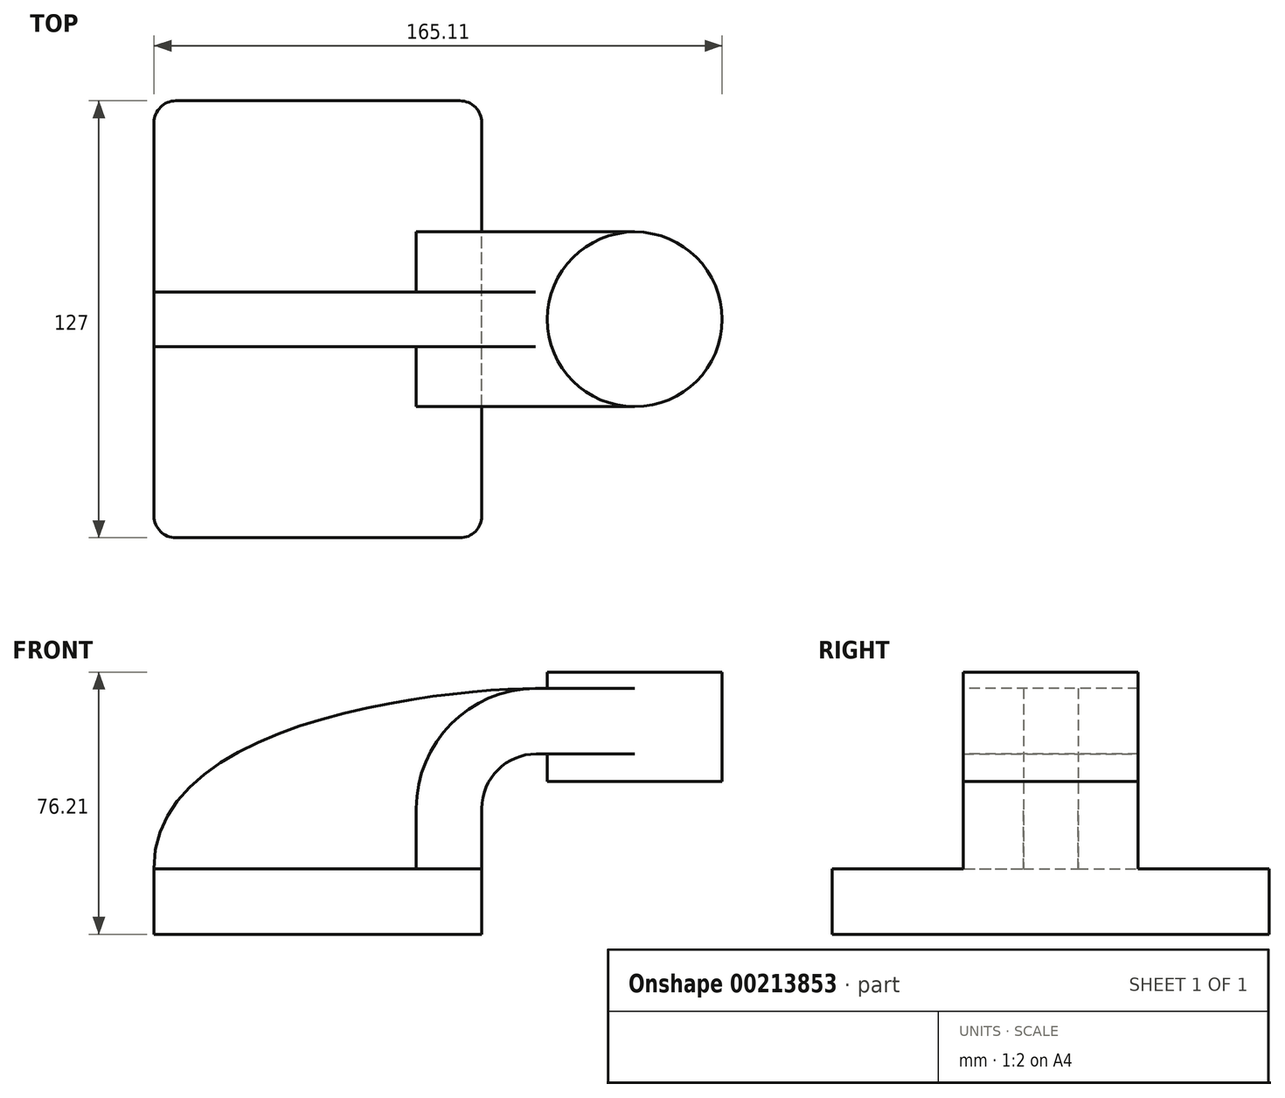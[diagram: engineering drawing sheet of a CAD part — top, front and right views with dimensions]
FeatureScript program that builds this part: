
annotation { "Feature Type Name" : "Feature", "Feature Type Description" : "" }
export const myFeature = defineFeature(function(context is Context, id is Id, definition is map)
    precondition{}
    {
        {
            var Q0;
            Q0=qCreatedBy(makeId("Front.planeOp"),FACE);
            var sketch = newSketch(context, id + "F0", { "sketchPlane" : qUnion([Q0])});
            skLineSegment(sketch, "E0.bottom", {"start": v(-47.63, 9.53) * mm, "end": v(47.63, 9.53) * mm});
            skLineSegment(sketch, "E0.top", {"start": v(-47.63, -9.52) * mm, "end": v(47.63, -9.52) * mm});
            skLineSegment(sketch, "E0.left", {"start": v(-47.63, 9.52) * mm, "end": v(-47.63, -9.52) * mm});
            skLineSegment(sketch, "E0.right", {"start": v(47.63, 9.53) * mm, "end": v(47.63, -9.53) * mm});
            skLineSegment(sketch, "E1", {"start": v(0, 9.52) * mm, "end": v(0, -9.52) * mm});
            skLineSegment(sketch, "E2", {"start": v(47.63, 9.53) * mm, "end": v(47.63, 27) * mm});
            skArc(sketch, "E3", {"start": v(63.5, 42.88) * mm, "mid": v(52.27, 38.23) * mm, "end": v(47.63, 27) * mm});
            skLineSegment(sketch, "E4", {"start": v(63.5, 42.88) * mm, "end": v(92.08, 42.88) * mm});
            skLineSegment(sketch, "E5.bottom", {"start": v(117.48, 34.93) * mm, "end": v(66.68, 34.93) * mm});
            skLineSegment(sketch, "E5.top", {"start": v(117.48, 66.67) * mm, "end": v(66.68, 66.67) * mm});
            skLineSegment(sketch, "E5.left", {"start": v(117.48, 34.93) * mm, "end": v(117.48, 66.68) * mm});
            skLineSegment(sketch, "E5.right", {"start": v(66.68, 34.93) * mm, "end": v(66.68, 66.68) * mm});
            skPoint(sketch, "E5.middle", {"position": v(92.08, 50.8) * mm});
            skLineSegment(sketch, "E6.0", {"start": v(63.5, 61.93) * mm, "end": v(92.08, 61.93) * mm});
            skArc(sketch, "E6.1", {"start": v(63.5, 61.93) * mm, "mid": v(38.8, 51.7) * mm, "end": v(28.58, 27) * mm});
            skLineSegment(sketch, "E6.2", {"start": v(28.57, 9.53) * mm, "end": v(28.57, 27) * mm});
            skLineSegment(sketch, "E7", {"start": v(92.08, 66.67) * mm, "end": v(92.08, 34.93) * mm});
            skFitSpline(sketch, "E8", {"points": [v(63.5, 61.93) * mm, v(-47.63, 9.52) * mm], "startDerivative": vector(-76.43, -0.25) * mm, "endDerivative": vector(1.6, -131) * mm});
            skSolve(sketch);
        }
        {
            var Q0;
            {var subQ0=sQuery(id+"F0.wireOp",EDGE,"E0.left");Q0=makeQuery(id+"F0.imprint","IMPRINT",FACE,{"disambiguationData":[TD([[makeQuery(id+"F0.imprint","IMPRINT",EDGE,{"derivedFrom":subQ0}),1.0]])]});}
            var Q1;
            {var subQ0=sQuery(id+"F0.wireOp",EDGE,"E0.right");Q1=makeQuery(id+"F0.imprint","IMPRINT",FACE,{"disambiguationData":[TD([[makeQuery(id+"F0.imprint","IMPRINT",EDGE,{"derivedFrom":subQ0}),-1.0]])]});}
            extrude(context, id + "F1", {"entities" : qUnion([Q0, Q1]), "endBound" : BoundingType.SYMMETRIC, "depth" : 127 * mm});
        }
        {
            var Q0;
            {var subQ4=sQuery(id+"F0.wireOp",EDGE,"E2");Q0=makeQuery(id+"F0.imprint","IMPRINT",FACE,{"disambiguationData":[TD([[makeQuery(id+"F0.imprint","IMPRINT",EDGE,{"derivedFrom":subQ4}),1.0]])]});}
            var Q1;
            {var subQ0=sQuery(id+"F0.wireOp",EDGE,"E7");var subQ1=sQuery(id+"F0.wireOp",EDGE,"E4");var subQ2=makeQuery(id+"F0.imprint","INTERSECT",VERTEX,{"derivedFrom":[subQ1,subQ0]});Q1=makeQuery(id+"F0.imprint","IMPRINT",FACE,{"disambiguationData":[TD([[makeQuery(id+"F0.imprint","IMPRINT",EDGE,{"disambiguationData":[TD([[subQ2,1.0]])],"derivedFrom":subQ1}),1.0]])]});}
            extrude(context, id + "F2", {"entities" : qUnion([Q0, Q1]), "operationType" : NewBodyOperationType.ADD, "endBound" : BoundingType.SYMMETRIC, "depth" : 50.8 * mm});
        }
        {
            var Q0;
            {var subQ0=sQuery(id+"F0.wireOp",EDGE,"E6.2");Q0=makeQuery(id+"F0.imprint","IMPRINT",FACE,{"disambiguationData":[TD([[makeQuery(id+"F0.imprint","IMPRINT",EDGE,{"derivedFrom":subQ0}),1.0]])]});}
            extrude(context, id + "F3", {"entities" : qUnion([Q0]), "operationType" : NewBodyOperationType.ADD, "endBound" : BoundingType.SYMMETRIC, "depth" : 15.88 * mm});
        }
        {
            var Q0;
            {var subQ4=sQuery(id+"F0.wireOp",EDGE,"E5.left");Q0=makeQuery(id+"F0.imprint","IMPRINT",FACE,{"disambiguationData":[TD([[makeQuery(id+"F0.imprint","IMPRINT",EDGE,{"derivedFrom":subQ4}),1.0]])]});}
            var Q1;
            Q1=sQuery(id+"F0.wireOp",EDGE,"E7");
            revolve(context, id + "F4", {"operationType" : NewBodyOperationType.ADD, "entities" : qUnion([Q0]), "axis" : qUnion([Q1]), "revolveType" : RevolveType.FULL});
        }
        {
            var Q0;
            Q0=makeQuery(id+"F1.opExtrude","CAP_EDGE",EDGE,{"disambiguationData":[OSD([sQuery(id+"F0.wireOp",EDGE,"E0.right")])],"isStart":false});
            var Q1;
            Q1=makeQuery(id+"F1.opExtrude","CAP_EDGE",EDGE,{"disambiguationData":[OSD([sQuery(id+"F0.wireOp",EDGE,"E0.left")])],"isStart":false});
            var Q2;
            Q2=makeQuery(id+"F1.opExtrude","CAP_EDGE",EDGE,{"disambiguationData":[OSD([sQuery(id+"F0.wireOp",EDGE,"E0.right")])],"isStart":true});
            var Q3;
            Q3=makeQuery(id+"F1.opExtrude","CAP_EDGE",EDGE,{"disambiguationData":[OSD([sQuery(id+"F0.wireOp",EDGE,"E0.left")])],"isStart":true});
            fillet(context, id + "F5", {"entities" : qUnion([Q0, Q1, Q2, Q3]), "radius" : 6.35 * mm, "tangentPropagation" : true, "allowEdgeOverflow" : false});
        }
    });
